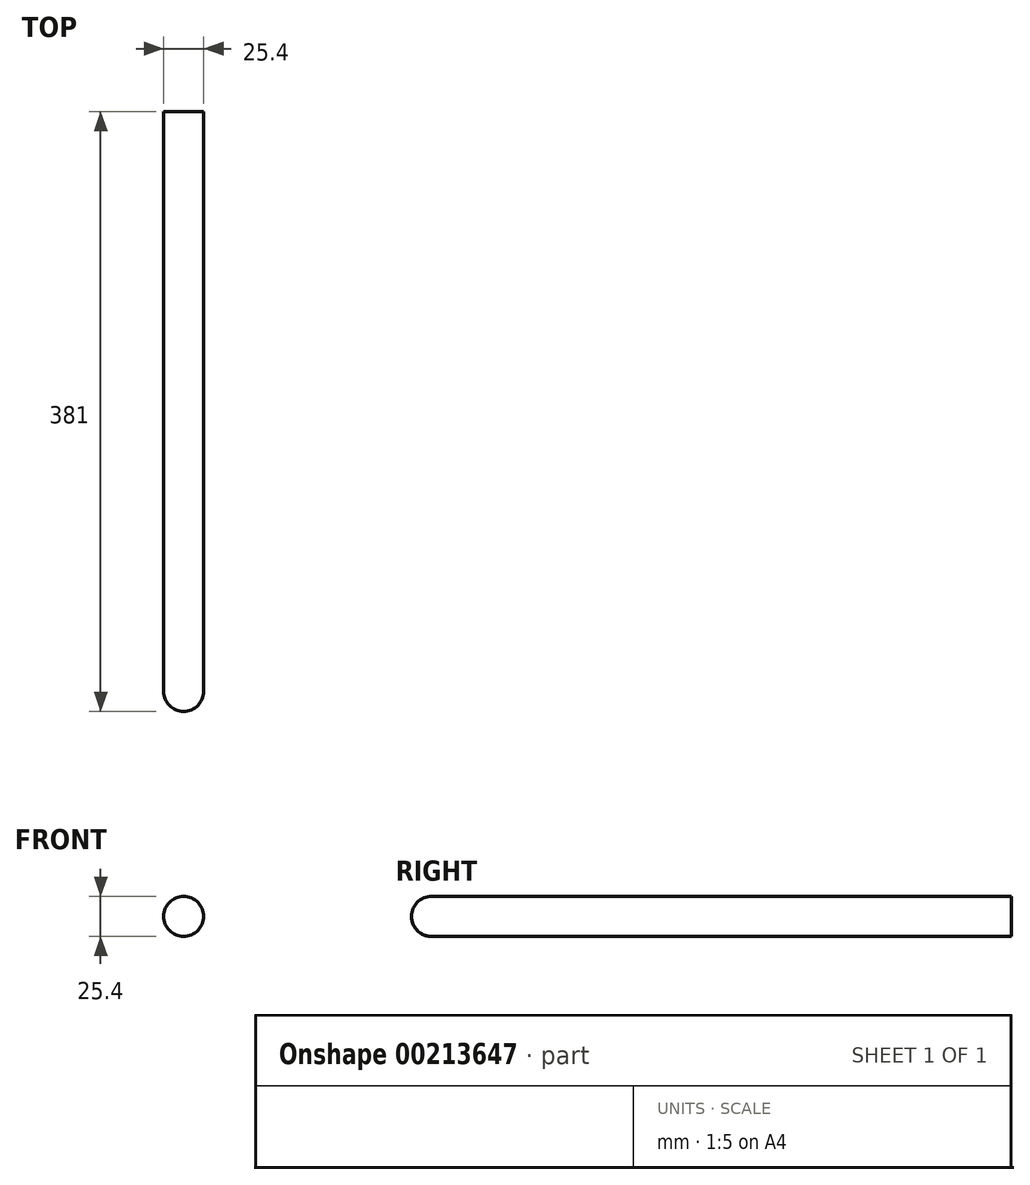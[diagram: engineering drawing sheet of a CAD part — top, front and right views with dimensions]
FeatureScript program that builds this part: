
annotation { "Feature Type Name" : "Feature", "Feature Type Description" : "" }
export const myFeature = defineFeature(function(context is Context, id is Id, definition is map)
    precondition{}
    {
        {
            var Q0;
            Q0=qCreatedBy(makeId("Front.planeOp"),FACE);
            var sketch = newSketch(context, id + "F0", { "sketchPlane" : qUnion([Q0])});
            skCircle(sketch, "E0", {"center": v(0, 0) * mm, "radius": 12.7 * mm});
            skSolve(sketch);
        }
        {
            var Q0;
            Q0=makeQuery(id+"F0.imprint","IMPRINT",FACE,{"disambiguationData":[TD([[makeQuery(id+"F0.imprint","IMPRINT",EDGE,{"derivedFrom":sQuery(id+"F0.wireOp",EDGE,"E0")}),1.0]])]});
            extrude(context, id + "F1", {"entities" : qUnion([Q0]), "oppositeDirection" : true, "depth" : 381 * mm});
        }
        {
            var Q0;
            Q0=makeQuery(id+"F1.opExtrude","CAP_EDGE",EDGE,{"disambiguationData":[OSD([sQuery(id+"F0.wireOp",EDGE,"E0")])],"isStart":true});
            fillet(context, id + "F2", {"entities" : qUnion([Q0]), "radius" : 12.7 * mm, "tangentPropagation" : true, "allowEdgeOverflow" : false});
        }
    });
